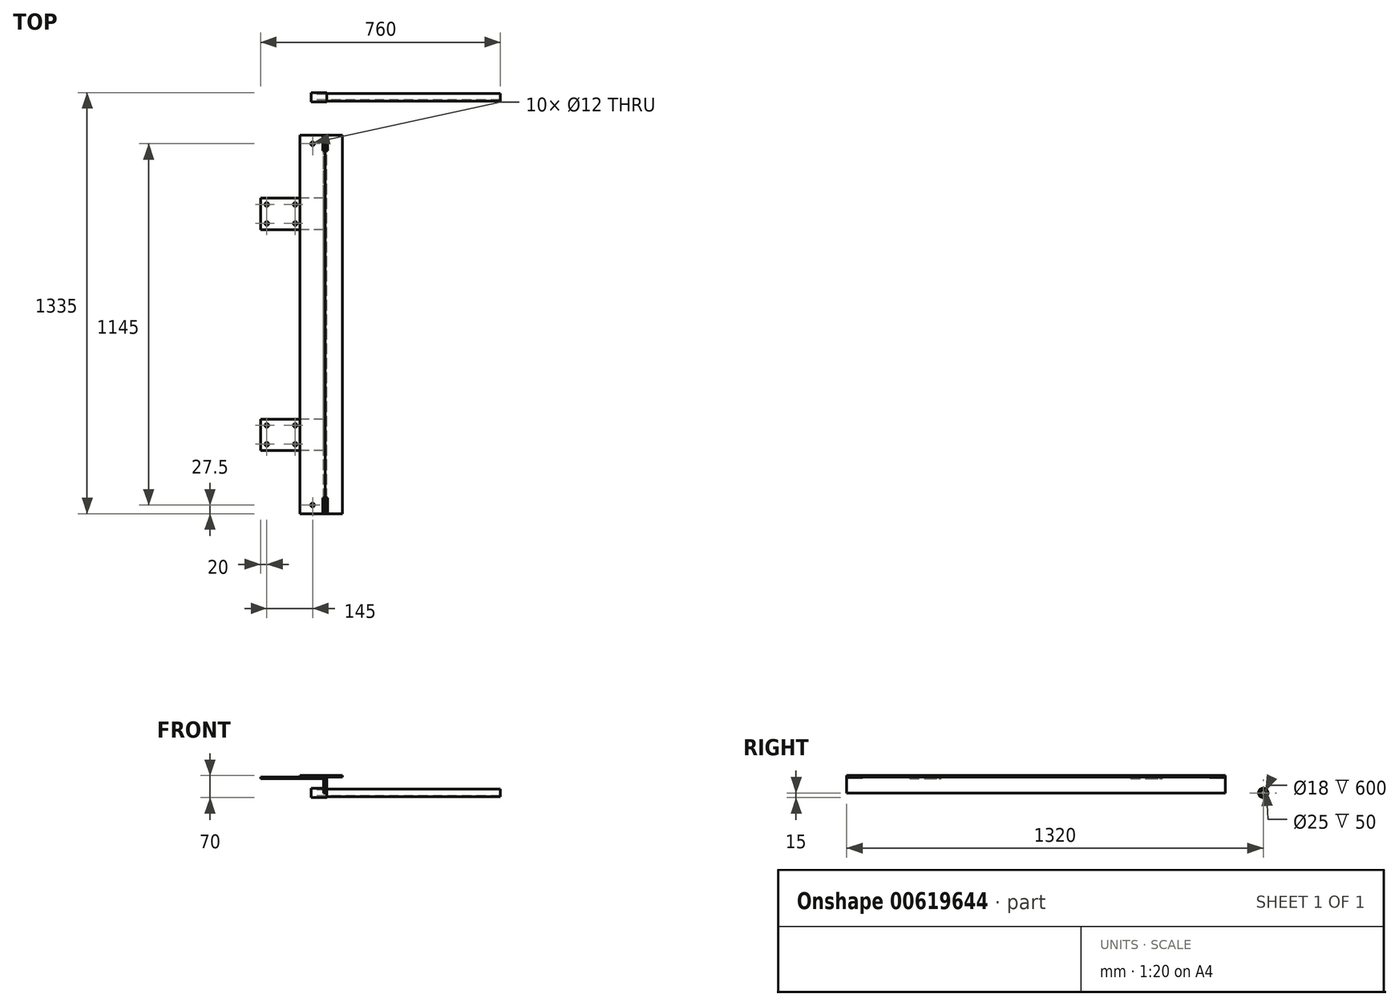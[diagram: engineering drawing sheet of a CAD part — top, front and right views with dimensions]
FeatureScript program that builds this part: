
annotation { "Feature Type Name" : "Feature", "Feature Type Description" : "" }
export const myFeature = defineFeature(function(context is Context, id is Id, definition is map)
    precondition{}
    {
        {
            var Q0;
            Q0=qCreatedBy(makeId("Front.planeOp"),FACE);
            var sketch = newSketch(context, id + "F0", { "sketchPlane" : qUnion([Q0])});
            skLineSegment(sketch, "E0", {"start": v(0, 0) * mm, "end": v(0, 50) * mm});
            skLineSegment(sketch, "E1", {"start": v(0, 50) * mm, "end": v(50, 50) * mm});
            skLineSegment(sketch, "E2", {"start": v(50, 50) * mm, "end": v(50, 55) * mm});
            skLineSegment(sketch, "E3", {"start": v(50, 55) * mm, "end": v(-5, 55) * mm});
            skLineSegment(sketch, "E4", {"start": v(-5, 55) * mm, "end": v(-5, 0) * mm});
            skLineSegment(sketch, "E5", {"start": v(-5, 0) * mm, "end": v(0, 0) * mm});
            skSolve(sketch);
        }
        {
            var Q0;
            Q0 = qSketchRegion(id + "F0", true);
            extrude(context, id + "F1", {"entities" : qUnion([Q0]), "depth" : 1200 * mm, "offsetDistance" : 25 * mm});
        }
        {
            var Q0;
            Q0=makeQuery(id+"F1.opExtrude","CAP_FACE",FACE,{"disambiguationData":[OSD([sQuery(id+"F0.wireOp",EDGE,"E0"),sQuery(id+"F0.wireOp",EDGE,"E1"),sQuery(id+"F0.wireOp",EDGE,"E2"),sQuery(id+"F0.wireOp",EDGE,"E3"),sQuery(id+"F0.wireOp",EDGE,"E4"),sQuery(id+"F0.wireOp",EDGE,"E5")])],"isStart":true});
            var sketch = newSketch(context, id + "F2", { "sketchPlane" : qUnion([Q0])});
            skCircle(sketch, "E6", {"center": v(5, 55) * mm, "radius": 7.5 * mm});
            skSolve(sketch);
        }
        {
            var Q0;
            Q0 = qSketchRegion(id + "F2", true);
            extrude(context, id + "F3", {"entities" : qUnion([Q0]), "operationType" : NewBodyOperationType.REMOVE, "oppositeDirection" : true, "depth" : 50 * mm, "offsetDistance" : 25 * mm});
        }
        {
            var Q0;
            Q0=makeQuery(id+"F1.opExtrude","CAP_FACE",FACE,{"disambiguationData":[OSD([sQuery(id+"F0.wireOp",EDGE,"E0"),sQuery(id+"F0.wireOp",EDGE,"E1"),sQuery(id+"F0.wireOp",EDGE,"E2"),sQuery(id+"F0.wireOp",EDGE,"E3"),sQuery(id+"F0.wireOp",EDGE,"E4"),sQuery(id+"F0.wireOp",EDGE,"E5")])],"isStart":false});
            var sketch = newSketch(context, id + "F4", { "sketchPlane" : qUnion([Q0])});
            skCircle(sketch, "E7", {"center": v(-5, 55) * mm, "radius": 7.5 * mm});
            skSolve(sketch);
        }
        {
            var Q0;
            Q0 = qSketchRegion(id + "F4", true);
            extrude(context, id + "F5", {"entities" : qUnion([Q0]), "operationType" : NewBodyOperationType.REMOVE, "oppositeDirection" : true, "depth" : 50 * mm, "offsetDistance" : 25 * mm});
        }
        {
            var Q0;
            Q0=qCreatedBy(makeId("Right.planeOp"),FACE);
            cPlane(context, id + "F6", {"entities" : qUnion([Q0]), "cplaneType" : CPlaneType.OFFSET, "offset" : 5 * mm, "oppositeDirection" : true, "width" : 150 * mm, "height" : 150 * mm});
        }
        {
            var Q0;
            Q0=makeQuery(id+"F1.opExtrude","SWEPT_BODY",BODY,{"disambiguationData":[OSD([sQuery(id+"F0.wireOp",EDGE,"E0"),sQuery(id+"F0.wireOp",EDGE,"E1"),sQuery(id+"F0.wireOp",EDGE,"E2"),sQuery(id+"F0.wireOp",EDGE,"E3"),sQuery(id+"F0.wireOp",EDGE,"E4"),sQuery(id+"F0.wireOp",EDGE,"E5")])]});
            var Q1;
            Q1=qCreatedBy(id+"F6.planeOp",FACE);
            mirror(context, id + "F7", {"entities" : qUnion([Q0]), "mirrorPlane" : qUnion([Q1])});
        }
        {
            var Q0;
            Q0=makeQuery(id+"F7.opPattern","COPY",FACE,{"derivedFrom":makeQuery(id+"F1.opExtrude","SWEPT_FACE",FACE,{"disambiguationData":[OSD([sQuery(id+"F0.wireOp",EDGE,"E3")])]}),"instanceName":"1"});
            var sketch = newSketch(context, id + "F8", { "sketchPlane" : qUnion([Q0])});
            skLineSegment(sketch, "E8.bottom", {"start": v(-60, 0) * mm, "end": v(-5, 0) * mm});
            skLineSegment(sketch, "E8.top", {"start": v(-60, -55) * mm, "end": v(-5, -55) * mm});
            skLineSegment(sketch, "E8.left", {"start": v(-60, 0) * mm, "end": v(-60, -55) * mm, "construction": true});
            skLineSegment(sketch, "E8.right", {"start": v(-5, 0) * mm, "end": v(-5, -55) * mm});
            skPoint(sketch, "E9", {"position": v(-32.5, -27.5) * mm});
            skPoint(sketch, "E9.positionSnap0", {"position": v(-60, -27.5) * mm});
            skPoint(sketch, "E9.positionSnap1", {"position": v(-32.5, 0) * mm});
            skLineSegment(sketch, "E10", {"start": v(-60, -600) * mm, "end": v(50, -600) * mm, "construction": true});
            skPoint(sketch, "E10.endSnap0", {"position": v(-5, -600) * mm});
            skCircle(sketch, "E11", {"center": v(-45, -27.5) * mm, "radius": 6 * mm});
            skCircle(sketch, "E12.MirrorC", {"center": v(-45, -1172.5) * mm, "radius": 6 * mm});
            skSolve(sketch);
        }
        {
            var Q0;
            Q0 = qSketchRegion(id + "F8", true);
            extrude(context, id + "F9", {"entities" : qUnion([Q0]), "operationType" : NewBodyOperationType.REMOVE, "oppositeDirection" : true, "depth" : 25 * mm, "offsetDistance" : 25 * mm});
        }
        {
            var Q0;
            Q0=makeQuery(id+"F7.opPattern","COPY",FACE,{"derivedFrom":makeQuery(id+"F1.opExtrude","SWEPT_FACE",FACE,{"disambiguationData":[OSD([sQuery(id+"F0.wireOp",EDGE,"E1")])]}),"instanceName":"1"});
            var sketch = newSketch(context, id + "F10", { "sketchPlane" : qUnion([Q0])});
            skPoint(sketch, "E13", {"position": v(-10, 200) * mm});
            skLineSegment(sketch, "E14.bottom", {"start": v(-10, 200) * mm, "end": v(-210, 200) * mm});
            skLineSegment(sketch, "E14.top", {"start": v(-10, 300) * mm, "end": v(-210, 300) * mm});
            skLineSegment(sketch, "E14.left", {"start": v(-10, 200) * mm, "end": v(-10, 300) * mm});
            skLineSegment(sketch, "E14.right", {"start": v(-210, 200) * mm, "end": v(-210, 300) * mm});
            skPoint(sketch, "E15", {"position": v(-190, 220) * mm});
            skPoint(sketch, "E16", {"position": v(-100, 220) * mm});
            skPoint(sketch, "E17", {"position": v(-190, 280) * mm});
            skPoint(sketch, "E18", {"position": v(-100, 280) * mm});
            skCircle(sketch, "E19", {"center": v(-190, 220) * mm, "radius": 6 * mm});
            skCircle(sketch, "E20", {"center": v(-190, 280) * mm, "radius": 6 * mm});
            skCircle(sketch, "E21", {"center": v(-100, 220) * mm, "radius": 6 * mm});
            skCircle(sketch, "E22", {"center": v(-100, 280) * mm, "radius": 6 * mm});
            skLineSegment(sketch, "E23", {"start": v(-60, 600) * mm, "end": v(-10, 600) * mm, "construction": true});
            skLineSegment(sketch, "E24.MirrorCS", {"start": v(-10, 1000) * mm, "end": v(-210, 1000) * mm});
            skLineSegment(sketch, "E25.MirrorCS", {"start": v(-210, 1000) * mm, "end": v(-210, 900) * mm});
            skLineSegment(sketch, "E26.MirrorCS", {"start": v(-10, 900) * mm, "end": v(-210, 900) * mm});
            skLineSegment(sketch, "E27.MirrorCS", {"start": v(-10, 1000) * mm, "end": v(-10, 900) * mm});
            skCircle(sketch, "E28.MirrorC", {"center": v(-100, 980) * mm, "radius": 6 * mm});
            skCircle(sketch, "E29.MirrorC", {"center": v(-100, 920) * mm, "radius": 6 * mm});
            skPoint(sketch, "E30.MirrorP", {"position": v(-190, 920) * mm});
            skPoint(sketch, "E31.MirrorP", {"position": v(-190, 980) * mm});
            skCircle(sketch, "E32.MirrorC", {"center": v(-190, 980) * mm, "radius": 6 * mm});
            skCircle(sketch, "E33.MirrorC", {"center": v(-190, 920) * mm, "radius": 6 * mm});
            skSolve(sketch);
        }
        {
            var Q0;
            Q0 = qSketchRegion(id + "F10", true);
            extrude(context, id + "F11", {"entities" : qUnion([Q0]), "depth" : 5 * mm, "offsetDistance" : 25 * mm});
        }
        {
            var Q0;
            Q0=qCreatedBy(makeId("Right.planeOp"),FACE);
            var sketch = newSketch(context, id + "F12", { "sketchPlane" : qUnion([Q0])});
            skPoint(sketch, "E34", {"position": v(120, 0) * mm});
            skCircle(sketch, "E35", {"center": v(120, 0) * mm, "radius": 15 * mm});
            skCircle(sketch, "E36", {"center": v(120, 0) * mm, "radius": 12.5 * mm});
            skSolve(sketch);
        }
        {
            var Q0;
            Q0 = qSketchRegion(id + "F12", true);
            extrude(context, id + "F13", {"entities" : qUnion([Q0]), "oppositeDirection" : true, "depth" : 50 * mm, "offsetDistance" : 25 * mm});
        }
        {
            var Q0;
            Q0=makeQuery(id+"F13.opExtrude","CAP_FACE",FACE,{"disambiguationData":[OSD([sQuery(id+"F12.wireOp",EDGE,"E35"),sQuery(id+"F12.wireOp",EDGE,"E36")])],"isStart":false});
            var sketch = newSketch(context, id + "F14", { "sketchPlane" : qUnion([Q0])});
            skCircle(sketch, "E37.0", {"center": v(-120, 0) * mm, "radius": 12.5 * mm});
            skCircle(sketch, "E38", {"center": v(-120, 0) * mm, "radius": 9 * mm});
            skSolve(sketch);
        }
        {
            var Q0;
            Q0 = qSketchRegion(id + "F14", true);
            extrude(context, id + "F15", {"entities" : qUnion([Q0]), "oppositeDirection" : true, "depth" : 600 * mm, "offsetDistance" : 25 * mm});
        }
        {
            var Q0;
            {var subQ0=sQuery(id+"F0.wireOp",EDGE,"E1");var subQ1=sQuery(id+"F0.wireOp",EDGE,"E2");var subQ2=sQuery(id+"F0.wireOp",EDGE,"E3");Q0=makeQuery(id+"F7.opPattern","COPY",FACE,{"derivedFrom":makeQuery(id+"F5.boolean.opBoolean","SPLIT",FACE,{"disambiguationData":[TD([makeQuery(id+"F1.opExtrude","SWEPT_FACE",FACE,{"disambiguationData":[OSD([subQ0])]})])],"derivedFrom":makeQuery(id+"F1.opExtrude","CAP_FACE",FACE,{"disambiguationData":[OSD([sQuery(id+"F0.wireOp",EDGE,"E0"),subQ0,subQ1,subQ2,sQuery(id+"F0.wireOp",EDGE,"E4"),sQuery(id+"F0.wireOp",EDGE,"E5")])],"isStart":false})}),"instanceName":"1"});}
            var sketch = newSketch(context, id + "F16", { "sketchPlane" : qUnion([Q0])});
            skLineSegment(sketch, "E39.0", {"start": v(-12.5, 55) * mm, "end": v(-5, 55) * mm});
            skLineSegment(sketch, "E40", {"start": v(-60, 55) * mm, "end": v(-85, 55) * mm});
            skPoint(sketch, "E40.endSnap0", {"position": v(-8.75, 55) * mm});
            skLineSegment(sketch, "E41", {"start": v(-85, 55) * mm, "end": v(-85, 50) * mm});
            skLineSegment(sketch, "E42", {"start": v(-85, 50) * mm, "end": v(-60, 50) * mm});
            skLineSegment(sketch, "E43", {"start": v(-60, 55) * mm, "end": v(-60, 50) * mm});
            skLineSegment(sketch, "E44.bottom", {"start": v(-60, 55) * mm, "end": v(-59, 55) * mm});
            skLineSegment(sketch, "E44.top", {"start": v(-60, 50) * mm, "end": v(-59, 50) * mm});
            skLineSegment(sketch, "E44.right", {"start": v(-59, 55) * mm, "end": v(-59, 50) * mm});
            skSolve(sketch);
        }
        {
            var Q0;
            Q0=makeQuery(id+"F16.imprint","IMPRINT",FACE,{"disambiguationData":[TD([[makeQuery(id+"F16.imprint","IMPRINT",EDGE,{"derivedFrom":sQuery(id+"F16.wireOp",EDGE,"E40")}),1.0]])]});
            var Q1;
            Q1=makeQuery(id+"F16.imprint","IMPRINT",FACE,{"disambiguationData":[TD([[makeQuery(id+"F16.imprint","IMPRINT",EDGE,{"derivedFrom":sQuery(id+"F16.wireOp",EDGE,"E44.bottom")}),-1.0]])]});
            extrude(context, id + "F17", {"entities" : qUnion([Q0, Q1]), "operationType" : NewBodyOperationType.ADD, "oppositeDirection" : true, "depth" : 1200 * mm, "offsetDistance" : 25 * mm});
        }
    });
